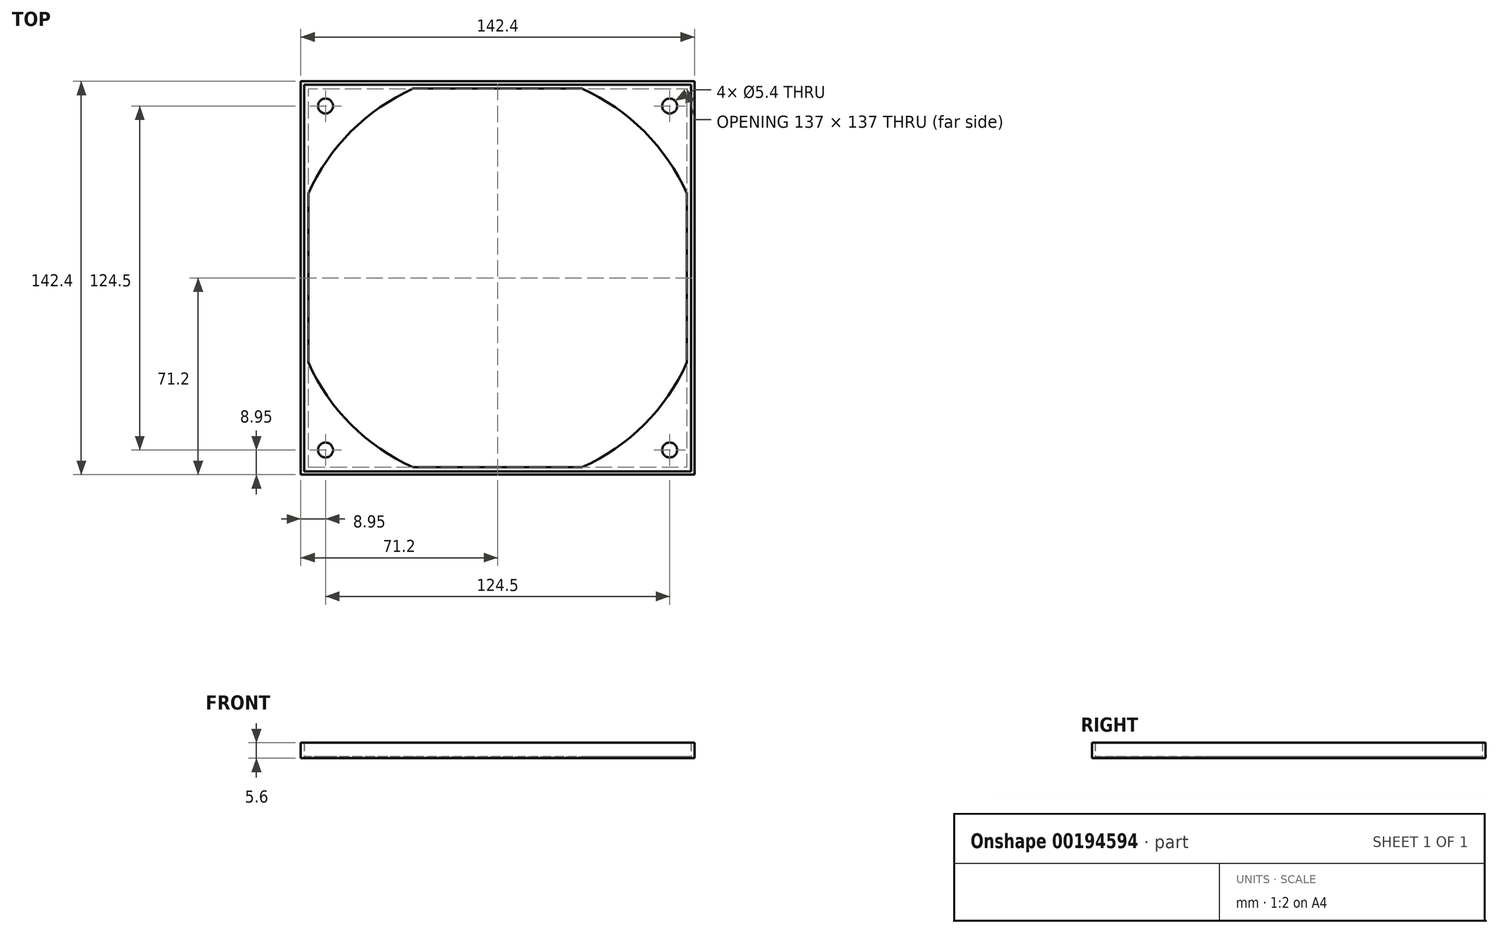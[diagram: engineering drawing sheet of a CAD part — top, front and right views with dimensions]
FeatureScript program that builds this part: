
annotation { "Feature Type Name" : "Feature", "Feature Type Description" : "" }
export const myFeature = defineFeature(function(context is Context, id is Id, definition is map)
    precondition{}
    {
        {
            var Q0;
            Q0=qCreatedBy(makeId("Top.planeOp"),FACE);
            var sketch = newSketch(context, id + "F0", { "sketchPlane" : qUnion([Q0])});
            skLineSegment(sketch, "E0.bottom", {"start": v(70, 70) * mm, "end": v(-70, 70) * mm, "construction": true});
            skLineSegment(sketch, "E0.top", {"start": v(70, -70) * mm, "end": v(-70, -70) * mm, "construction": true});
            skLineSegment(sketch, "E0.left", {"start": v(70, 70) * mm, "end": v(70, -70) * mm, "construction": true});
            skLineSegment(sketch, "E0.right", {"start": v(-70, 70) * mm, "end": v(-70, -70) * mm, "construction": true});
            skPoint(sketch, "E0.middle", {"position": v(0, 0) * mm});
            skLineSegment(sketch, "E1.bottom", {"start": v(62.25, 62.25) * mm, "end": v(-62.25, 62.25) * mm, "construction": true});
            skLineSegment(sketch, "E1.top", {"start": v(62.25, -62.25) * mm, "end": v(-62.25, -62.25) * mm, "construction": true});
            skLineSegment(sketch, "E1.left", {"start": v(62.25, 62.25) * mm, "end": v(62.25, -62.25) * mm, "construction": true});
            skLineSegment(sketch, "E1.right", {"start": v(-62.25, 62.25) * mm, "end": v(-62.25, -62.25) * mm, "construction": true});
            skLineSegment(sketch, "E2.bottom", {"start": v(68.5, 68.5) * mm, "end": v(-68.5, 68.5) * mm, "construction": true});
            skLineSegment(sketch, "E2.top", {"start": v(68.5, -68.5) * mm, "end": v(-68.5, -68.5) * mm, "construction": true});
            skLineSegment(sketch, "E2.left", {"start": v(68.5, 68.5) * mm, "end": v(68.5, -68.5) * mm, "construction": true});
            skLineSegment(sketch, "E2.right", {"start": v(-68.5, 68.5) * mm, "end": v(-68.5, -68.5) * mm, "construction": true});
            skArc(sketch, "E3", {"start": v(30.54, 68.5) * mm, "mid": v(53.03, 53.03) * mm, "end": v(68.5, 30.54) * mm, "construction": true});
            skArc(sketch, "E4", {"start": v(-30.54, 68.5) * mm, "mid": v(-53.03, 53.03) * mm, "end": v(-68.5, 30.54) * mm, "construction": true});
            skArc(sketch, "E5", {"start": v(-68.5, -30.54) * mm, "mid": v(-53.03, -53.03) * mm, "end": v(-30.54, -68.5) * mm, "construction": true});
            skArc(sketch, "E6", {"start": v(68.5, -30.54) * mm, "mid": v(53.03, -53.03) * mm, "end": v(30.54, -68.5) * mm, "construction": true});
            skCircle(sketch, "E7", {"center": v(-62.25, 62.25) * mm, "radius": 2.6 * mm, "construction": true});
            skCircle(sketch, "E8", {"center": v(62.25, 62.25) * mm, "radius": 2.6 * mm, "construction": true});
            skCircle(sketch, "E9", {"center": v(-62.25, -62.25) * mm, "radius": 2.6 * mm, "construction": true});
            skCircle(sketch, "E10", {"center": v(62.25, -62.25) * mm, "radius": 2.6 * mm, "construction": true});
            skSolve(sketch);
        }
        {
            var Q0;
            Q0=qCreatedBy(makeId("Top.planeOp"),FACE);
            var sketch = newSketch(context, id + "F1", { "sketchPlane" : qUnion([Q0])});
            skLineSegment(sketch, "E11.0", {"start": v(70, 70) * mm, "end": v(-70, 70) * mm, "construction": true});
            skLineSegment(sketch, "E12.0", {"start": v(-70, 70) * mm, "end": v(-70, -70) * mm, "construction": true});
            skLineSegment(sketch, "E13.0", {"start": v(70, -70) * mm, "end": v(-70, -70) * mm, "construction": true});
            skLineSegment(sketch, "E14.0", {"start": v(70, 70) * mm, "end": v(70, -70) * mm, "construction": true});
            skLineSegment(sketch, "E15.0", {"start": v(71.2, 71.2) * mm, "end": v(-71.2, 71.2) * mm});
            skLineSegment(sketch, "E15.1", {"start": v(71.2, 71.2) * mm, "end": v(71.2, -71.2) * mm});
            skLineSegment(sketch, "E15.2", {"start": v(71.2, -71.2) * mm, "end": v(-71.2, -71.2) * mm});
            skLineSegment(sketch, "E15.3", {"start": v(-71.2, 71.2) * mm, "end": v(-71.2, -71.2) * mm});
            skArc(sketch, "E16.0", {"start": v(-30.54, 68.5) * mm, "mid": v(-53.03, 53.03) * mm, "end": v(-68.5, 30.54) * mm});
            skArc(sketch, "E17.0", {"start": v(30.54, 68.5) * mm, "mid": v(53.03, 53.03) * mm, "end": v(68.5, 30.54) * mm});
            skArc(sketch, "E18.0", {"start": v(68.5, -30.54) * mm, "mid": v(53.03, -53.03) * mm, "end": v(30.54, -68.5) * mm});
            skArc(sketch, "E19.0", {"start": v(-68.5, -30.54) * mm, "mid": v(-53.03, -53.03) * mm, "end": v(-30.54, -68.5) * mm});
            skLineSegment(sketch, "E20", {"start": v(-30.54, 68.5) * mm, "end": v(30.54, 68.5) * mm});
            skLineSegment(sketch, "E21", {"start": v(68.5, 30.54) * mm, "end": v(68.5, -30.54) * mm});
            skLineSegment(sketch, "E22", {"start": v(-68.5, 30.54) * mm, "end": v(-68.5, -30.54) * mm});
            skLineSegment(sketch, "E23", {"start": v(-30.54, -68.5) * mm, "end": v(30.54, -68.5) * mm});
            skSolve(sketch);
        }
        {
            var Q0;
            Q0=qCreatedBy(makeId("Top.planeOp"),FACE);
            var sketch = newSketch(context, id + "F2", { "sketchPlane" : qUnion([Q0])});
            skLineSegment(sketch, "E24.0", {"start": v(71.2, 71.2) * mm, "end": v(-71.2, 71.2) * mm});
            skLineSegment(sketch, "E25.0", {"start": v(-71.2, 71.2) * mm, "end": v(-71.2, -71.2) * mm});
            skLineSegment(sketch, "E26.0", {"start": v(71.2, 71.2) * mm, "end": v(71.2, -71.2) * mm});
            skLineSegment(sketch, "E27.0", {"start": v(71.2, -71.2) * mm, "end": v(-71.2, -71.2) * mm});
            skLineSegment(sketch, "E28.0", {"start": v(70, 70) * mm, "end": v(70, -70) * mm});
            skLineSegment(sketch, "E29.0", {"start": v(70, -70) * mm, "end": v(-70, -70) * mm});
            skLineSegment(sketch, "E30.0", {"start": v(-70, 70) * mm, "end": v(-70, -70) * mm});
            skLineSegment(sketch, "E31.0", {"start": v(70, 70) * mm, "end": v(-70, 70) * mm});
            skSolve(sketch);
        }
        {
            var Q0;
            Q0=qCreatedBy(makeId("Top.planeOp"),FACE);
            var sketch = newSketch(context, id + "F3", { "sketchPlane" : qUnion([Q0])});
            skCircle(sketch, "E32.0", {"center": v(-62.25, 62.25) * mm, "radius": 2.6 * mm, "construction": true});
            skCircle(sketch, "E33.0", {"center": v(62.25, 62.25) * mm, "radius": 2.6 * mm, "construction": true});
            skCircle(sketch, "E34.0", {"center": v(62.25, -62.25) * mm, "radius": 2.6 * mm, "construction": true});
            skCircle(sketch, "E35.0", {"center": v(-62.25, -62.25) * mm, "radius": 2.6 * mm, "construction": true});
            skCircle(sketch, "E36.0", {"center": v(62.25, 62.25) * mm, "radius": 2.7 * mm});
            skCircle(sketch, "E37.0", {"center": v(-62.25, 62.25) * mm, "radius": 2.7 * mm});
            skCircle(sketch, "E38.0", {"center": v(-62.25, -62.25) * mm, "radius": 2.7 * mm});
            skCircle(sketch, "E39.0", {"center": v(62.25, -62.25) * mm, "radius": 2.7 * mm});
            skSolve(sketch);
        }
        {
            var Q0;
            Q0 = qSketchRegion(id + "F1", true);
            extrude(context, id + "F4", {"entities" : qUnion([Q0]), "oppositeDirection" : true, "depth" : 0.6 * mm});
        }
        {
            var Q0;
            Q0 = qSketchRegion(id + "F2", true);
            extrude(context, id + "F5", {"entities" : qUnion([Q0]), "operationType" : NewBodyOperationType.ADD, "depth" : 5 * mm});
        }
        {
            var Q0;
            Q0 = qSketchRegion(id + "F3", true);
            extrude(context, id + "F6", {"entities" : qUnion([Q0]), "operationType" : NewBodyOperationType.REMOVE, "endBound" : BoundingType.THROUGH_ALL, "oppositeDirection" : true, "depth" : 25 * mm});
        }
    });
